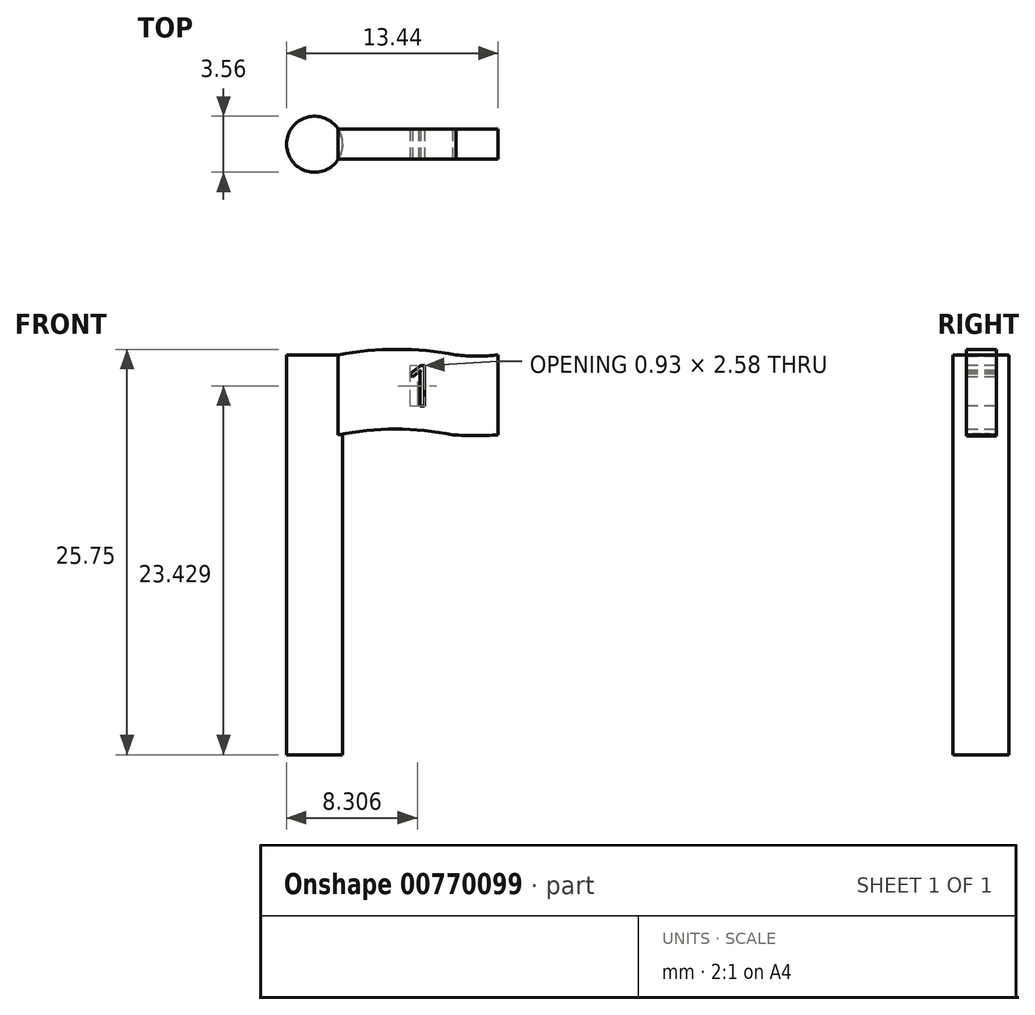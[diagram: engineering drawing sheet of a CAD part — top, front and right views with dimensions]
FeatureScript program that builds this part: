
annotation { "Feature Type Name" : "Feature", "Feature Type Description" : "" }
export const myFeature = defineFeature(function(context is Context, id is Id, definition is map)
    precondition{}
    {
        {
            var Q0;
            Q0=qCreatedBy(makeId("Front.planeOp"),FACE);
            var sketch = newSketch(context, id + "F0", { "sketchPlane" : qUnion([Q0])});
            skArc(sketch, "E0", {"start": v(7.48, 0) * mm, "mid": v(3.74, 0.35) * mm, "end": v(0, 0) * mm});
            skArc(sketch, "E1", {"start": v(7.48, 0) * mm, "mid": v(8.82, -0.09) * mm, "end": v(10.16, 0) * mm});
            skLineSegment(sketch, "E2", {"start": v(10.16, 0) * mm, "end": v(10.16, -5.08) * mm});
            skArc(sketch, "E3", {"start": v(7.29, -5.08) * mm, "mid": v(8.72, -5.14) * mm, "end": v(10.16, -5.08) * mm});
            skArc(sketch, "E4", {"start": v(7.29, -5.08) * mm, "mid": v(3.64, -4.72) * mm, "end": v(0, -5.08) * mm});
            skLineSegment(sketch, "E5", {"start": v(0, 0) * mm, "end": v(0, -5.08) * mm});
            skSolve(sketch);
        }
        {
            var Q0;
            Q0=makeQuery(id+"F0.imprint","IMPRINT",FACE,{"disambiguationData":[TD([[makeQuery(id+"F0.imprint","IMPRINT",EDGE,{"derivedFrom":sQuery(id+"F0.wireOp",EDGE,"E0")}),1.0]])]});
            extrude(context, id + "F1", {"entities" : qUnion([Q0]), "depth" : 1.9 * mm, "offsetDistance" : 25.4 * mm});
        }
        {
            var Q0;
            Q0=qCreatedBy(makeId("Top.planeOp"),FACE);
            var sketch = newSketch(context, id + "F2", { "sketchPlane" : qUnion([Q0])});
            skCircle(sketch, "E6", {"center": v(-1.5, -0.95) * mm, "radius": 1.78 * mm});
            skSolve(sketch);
        }
        {
            var Q0;
            Q0 = qSketchRegion(id + "F2", true);
            extrude(context, id + "F3", {"entities" : qUnion([Q0]), "operationType" : NewBodyOperationType.ADD, "oppositeDirection" : true, "depth" : 25.4 * mm, "offsetDistance" : 25.4 * mm});
        }
        {
            var Q0;
            Q0=makeQuery(id+"F1.opExtrude","CAP_FACE",FACE,{"disambiguationData":[OSD([sQuery(id+"F0.wireOp",EDGE,"E0"),sQuery(id+"F0.wireOp",EDGE,"E1"),sQuery(id+"F0.wireOp",EDGE,"E2"),sQuery(id+"F0.wireOp",EDGE,"E3"),sQuery(id+"F0.wireOp",EDGE,"E4"),sQuery(id+"F0.wireOp",EDGE,"E5")])],"isStart":false});
            var sketch = newSketch(context, id + "F4", { "sketchPlane" : qUnion([Q0])});
            skText(sketch, "E7", { "text": "1", "fontName": "OpenSans-Regular.ttf"});
            const initialGuessF4  = {"E7": [0.00423, -0.00326, 1, 0, 0.0026]};
            skSetInitialGuess(sketch, initialGuessF4);
            skSolve(sketch);
        }
        {
            var Q0;
            Q0 = qSketchRegion(id + "F4", true);
            extrude(context, id + "F5", {"entities" : qUnion([Q0]), "operationType" : NewBodyOperationType.REMOVE, "endBound" : BoundingType.THROUGH_ALL, "oppositeDirection" : true, "depth" : 1.27 * mm, "offsetDistance" : 25.4 * mm});
        }
    });
